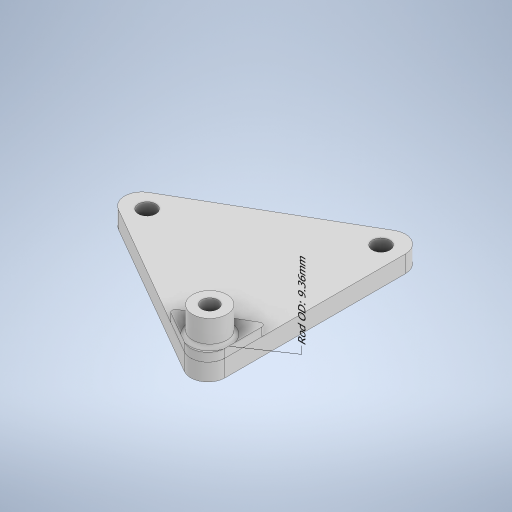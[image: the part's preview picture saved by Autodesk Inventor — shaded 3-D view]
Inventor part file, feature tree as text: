
AUTODESK INVENTOR PART (.ipt)
format: ipt  version: 2023 (Build 270158000, 158)  size: 311,296 bytes
history: native  units: mm
features: other x3, extrude x3, sketch x3, fillet x1
ambient origin geometry x8: Origin, YZ Plane, XZ Plane, XY Plane, X Axis, Y Axis, Z Axis, Center Point
bodies: Solid1 (feature_tree)
feature tree (10):
  other  "Annotations"
  extrude  "Extrusion1"  Depth=100.0mm
  extrude  "Extrusion2"  Depth=10.0mm
  extrude  "Extrusion3"  Depth=2.0mm
  fillet  "Fillet1"  Radius=25.0mm
  sketch  "Sketch1"  dims[d0=10.254mm d1=100.0mm]
  sketch  "Sketch2"  dims[d2=140.0mm d3=10.0mm]
  other  "Tight_Bushing"
  sketch  "Sketch3"  dims[d4=10.0mm d5=0.0mm d6=25.0mm d7=25.0mm d8=2.0mm d11=9.487mm d12=5.0mm d13=0.0mm d14=20.0mm d15=15.0mm d16=0.0mm d17=2.0mm]
  other  "Leader Text 1"
